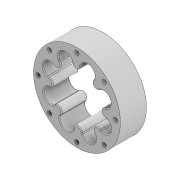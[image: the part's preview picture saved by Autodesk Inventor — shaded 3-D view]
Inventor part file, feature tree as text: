
AUTODESK INVENTOR PART (.ipt)
format: ipt  version: 2020.3 (Build 243373010, 373A)  size: 370,688 bytes
history: native  units: mm
features: sketch x3, hole x2, pattern_circular x2, fillet x2, extrude x1, projected_geometry x1
ambient origin geometry x8: Origin, YZ Plane, XZ Plane, XY Plane, X Axis, Y Axis, Z Axis, Center Point
bodies: Solid1 (feature_tree)
feature tree (11):
  extrude  "Extrusion1"  Depth=30.0mm
  hole  "Hole1"  [1 undecoded]
  hole  "Hole2"  [1 undecoded]
  pattern_circular  "Circular Pattern1"  [2 undecoded]
  fillet  "Fillet2"  Radius=5.0mm
  pattern_circular  "Circular Pattern2"  Count=8 Angle=360.0deg
  fillet  "Fillet3"  [1 undecoded]
  sketch  "Sketch2"  dims[d2=30.0mm d3=0.0mm d6=100.0mm]
  sketch  "Sketch4"  dims[d9=100.0mm d10=85.0mm]
  sketch  "Sketch5"  dims[d11=80.0mm d13=360.0deg d15=4.458734mm d16=10.0mm d17=4.0mm d18=2.0mm d19=14.3117mm d20=10.0mm d21=20.594885mm d23=5.0mm d24=6.0mm d25=8.0mm d26=5.0mm d27=90.0deg d28=8.0mm d29=20.594885mm d30=80.0mm d31=360.0deg d33=44.5mm d35=5.0mm d36=80.0mm d37=360.0deg d39=1.0mm]
  projected_geometry  "Projected Loop1"
note: 5 required parameter values undecoded (feature->parameter linkage not recoverable at this tier; creation-order binding heuristic only, values carry confidence <= 0.55)
